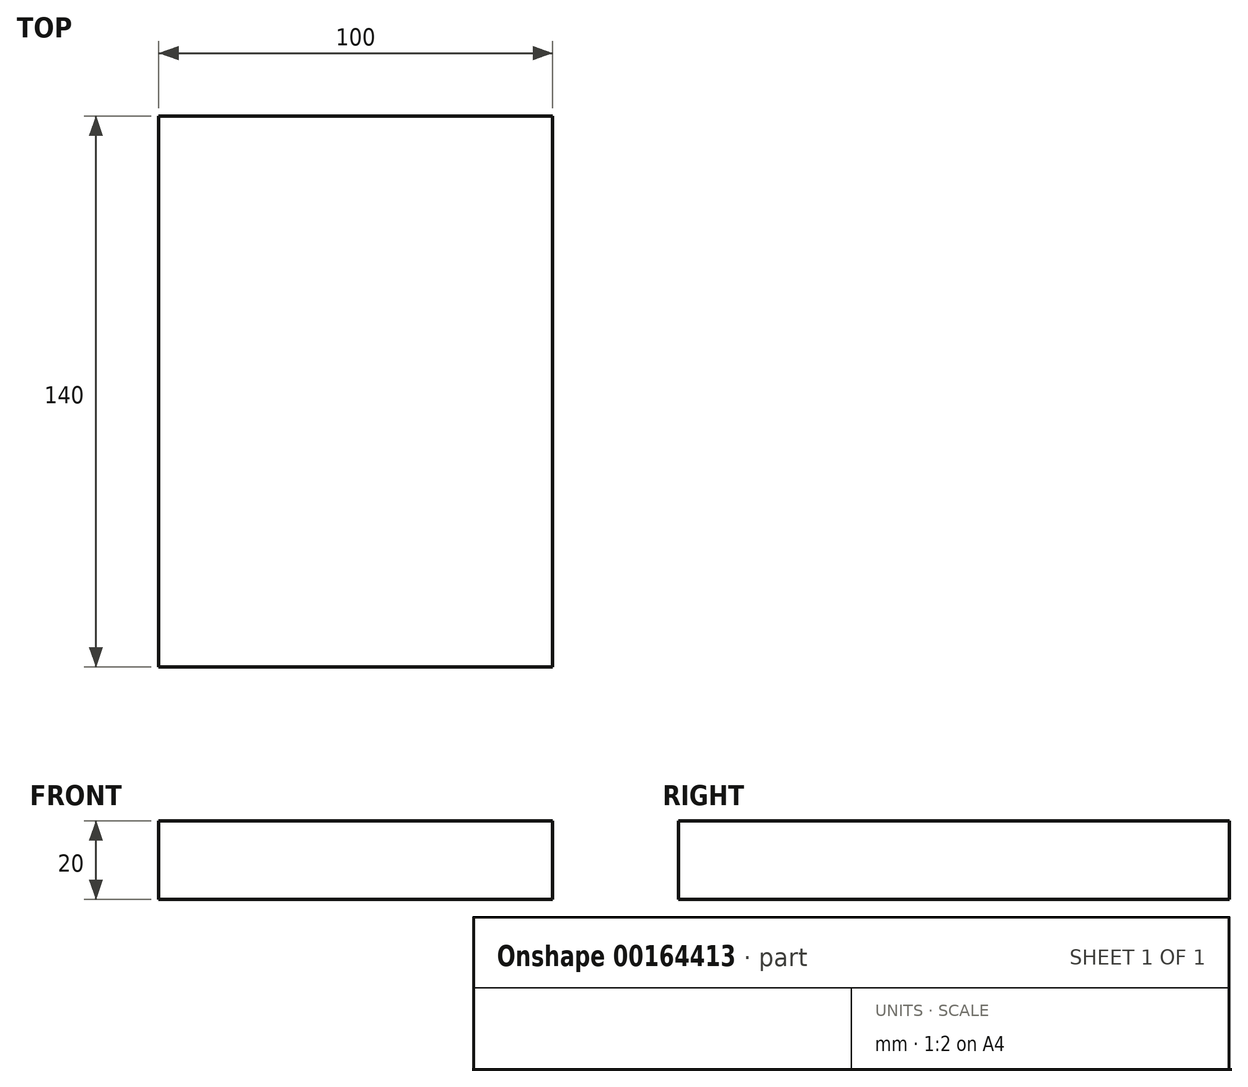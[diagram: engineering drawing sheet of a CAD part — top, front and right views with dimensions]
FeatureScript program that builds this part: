
annotation { "Feature Type Name" : "Feature", "Feature Type Description" : "" }
export const myFeature = defineFeature(function(context is Context, id is Id, definition is map)
    precondition{}
    {
        {
            var Q0;
            Q0=qCreatedBy(makeId("Front.planeOp"),FACE);
            var sketch = newSketch(context, id + "F0", { "sketchPlane" : qUnion([Q0])});
            skLineSegment(sketch, "E0.bottom", {"start": v(-50, 10) * mm, "end": v(50, 10) * mm});
            skLineSegment(sketch, "E0.top", {"start": v(-50, -10) * mm, "end": v(50, -10) * mm});
            skLineSegment(sketch, "E0.left", {"start": v(-50, 10) * mm, "end": v(-50, -10) * mm});
            skLineSegment(sketch, "E0.right", {"start": v(50, 10) * mm, "end": v(50, -10) * mm});
            skPoint(sketch, "E0.middle", {"position": v(0, 0) * mm});
            skLineSegment(sketch, "E1.bottom", {"start": v(66.8, 63.72) * mm, "end": v(109.54, 63.72) * mm});
            skLineSegment(sketch, "E1.top", {"start": v(66.8, 34.98) * mm, "end": v(109.54, 34.98) * mm});
            skLineSegment(sketch, "E1.left", {"start": v(66.8, 63.72) * mm, "end": v(66.8, 34.98) * mm});
            skLineSegment(sketch, "E1.right", {"start": v(109.54, 63.72) * mm, "end": v(109.54, 34.98) * mm});
            skPoint(sketch, "E1.middle", {"position": v(88.17, 49.35) * mm});
            skLineSegment(sketch, "E2", {"start": v(50, 10) * mm, "end": v(50, 35) * mm});
            skArc(sketch, "E3", {"start": v(50, 35) * mm, "mid": v(53.13, 44.17) * mm, "end": v(61.22, 49.51) * mm});
            skLineSegment(sketch, "E4", {"start": v(61.22, 49.51) * mm, "end": v(81.22, 49.51) * mm});
            skLineSegment(sketch, "E5.0", {"start": v(60.1, 59.51) * mm, "end": v(81.18, 59.51) * mm});
            skArc(sketch, "E5.1", {"start": v(40, 35) * mm, "mid": v(45.67, 50.85) * mm, "end": v(60.1, 59.51) * mm});
            skLineSegment(sketch, "E5.2", {"start": v(40, 10) * mm, "end": v(40, 35) * mm});
            skSolve(sketch);
        }
        {
            var Q0;
            Q0=makeQuery(id+"F0.imprint","IMPRINT",FACE,{"disambiguationData":[TD([[makeQuery(id+"F0.imprint","IMPRINT",EDGE,{"derivedFrom":sQuery(id+"F0.wireOp",EDGE,"E0.top")}),1.0]])]});
            extrude(context, id + "F1", {"entities" : qUnion([Q0]), "endBound" : BoundingType.SYMMETRIC, "depth" : 140 * mm});
        }
    });
